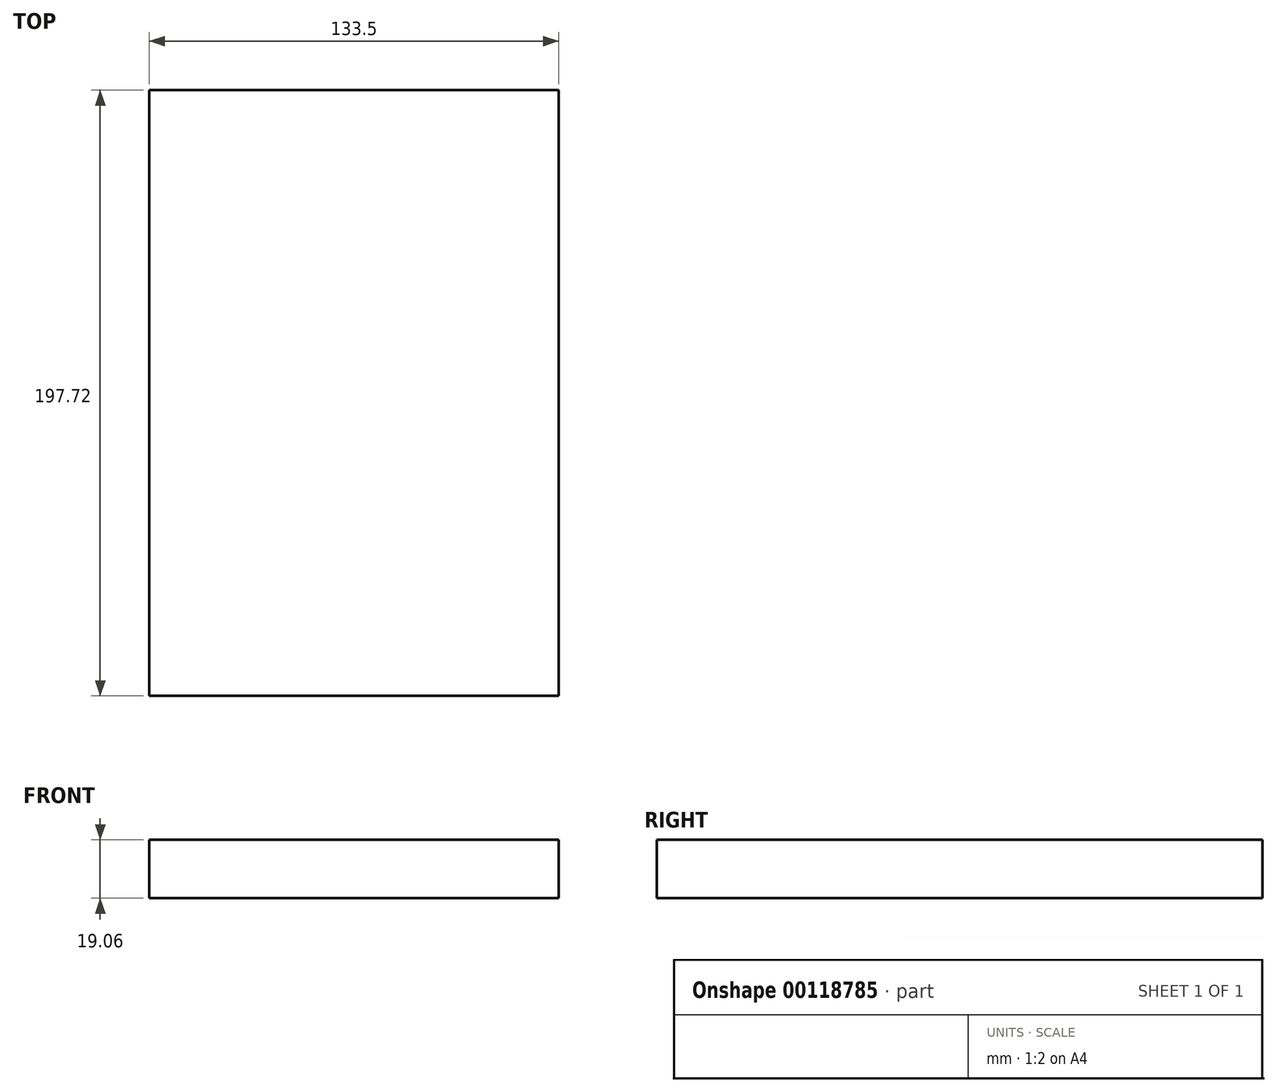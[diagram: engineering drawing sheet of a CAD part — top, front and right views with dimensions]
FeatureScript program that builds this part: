
annotation { "Feature Type Name" : "Feature", "Feature Type Description" : "" }
export const myFeature = defineFeature(function(context is Context, id is Id, definition is map)
    precondition{}
    {
        {
            var Q0;
            Q0=qCreatedBy(makeId("Top.planeOp"),FACE);
            var sketch = newSketch(context, id + "F2", { "sketchPlane" : qUnion([Q0])});
            skLineSegment(sketch, "E0.bottom", {"start": v(66.75, -98.86) * mm, "end": v(-66.75, -98.86) * mm});
            skLineSegment(sketch, "E0.top", {"start": v(66.75, 98.86) * mm, "end": v(-66.75, 98.86) * mm});
            skLineSegment(sketch, "E0.left", {"start": v(66.75, -98.86) * mm, "end": v(66.75, 98.86) * mm});
            skLineSegment(sketch, "E0.right", {"start": v(-66.75, -98.86) * mm, "end": v(-66.75, 98.86) * mm});
            skPoint(sketch, "E0.middle", {"position": v(0, 0) * mm});
            skSolve(sketch);
        }
        {
            var Q0;
            Q0=makeQuery(id+"F2.imprint","IMPRINT",FACE,{"disambiguationData":[TD([[makeQuery(id+"F2.imprint","IMPRINT",EDGE,{"derivedFrom":sQuery(id+"F2.wireOp",EDGE,"E0.bottom")}),-1.0]])]});
            extrude(context, id + "F0", {"entities" : qUnion([Q0]), "endBound" : BoundingType.SYMMETRIC, "depth" : 19.05 * mm});
        }
    });
